# Revit family: Control-Lutron-Athena-Q-TOUCH5
name_source: partatom
category: Lighting Devices
revit_build: Autodesk Revit 2018 (Build: 20170223_1515(x64)
units: mm (PartAtom-declared; Revit-internal decimal feet)

## family parameters
Cut with Voids When Loaded = No
Host = Face
Maintain Annotation Orientation = Yes
OmniClass Number = 23.85.80.11.27
OmniClass Title = Lighting Controls
Part Type = Switch
Room Calculation Point = No
Round Connector Dimension = Use Diameter
Shared = No

## types (1)
- Q-TOUCH5-WH
    Assembly Code = D5020120
    Cost = 0 $
    Default Elevation = 5' - 0"
    Description = Athena Touchscreen
    Environment = Ambient operating temperature: 32 °F to 104°F (0 °C to 40 °C) 5% to 90% relative humidity (non-condensing). Indoor use only. IP20 Rating
    Finish = Plastic - Lutron - White - Matte
    Instruction Sheet Link = https://www.lutron.com
    Manufacturer = Lutron Electronics Co., Inc
    Manufacturer Fax Number = 610-282-1243
    Model = Q-TOUCH5-WH
    Overall Depth = 0' - 0 5/8"
    Overall Height = 0' - 3 13/16"
    Overall Width = 0' - 5 1/2"
    Performance URL = https://www.lutron.com
    Product Documentation Link = https://www.lutron.com
    Product Name = Athena Touchscreen
    Product Page URL = https://www.lutron.com
    Series = Athena
    URL = http://www.lutron.com
    Version = 2018 - v1.0a
    Video Link = https://www.youtube.com
    Voltage = 0 V
    Voltage Comment = Must be powered by an IEEE 802.3af-2003 or 802.3at-2009 compliant Power over Ethernet (PoE) supply, Lutron model Q-POE-PNL or by others.
    Warranty URL = http://www.lutron.com

## geometry (parser evidence)
native form markers: Sweep x3
no freeform markers — native parametric forms only
